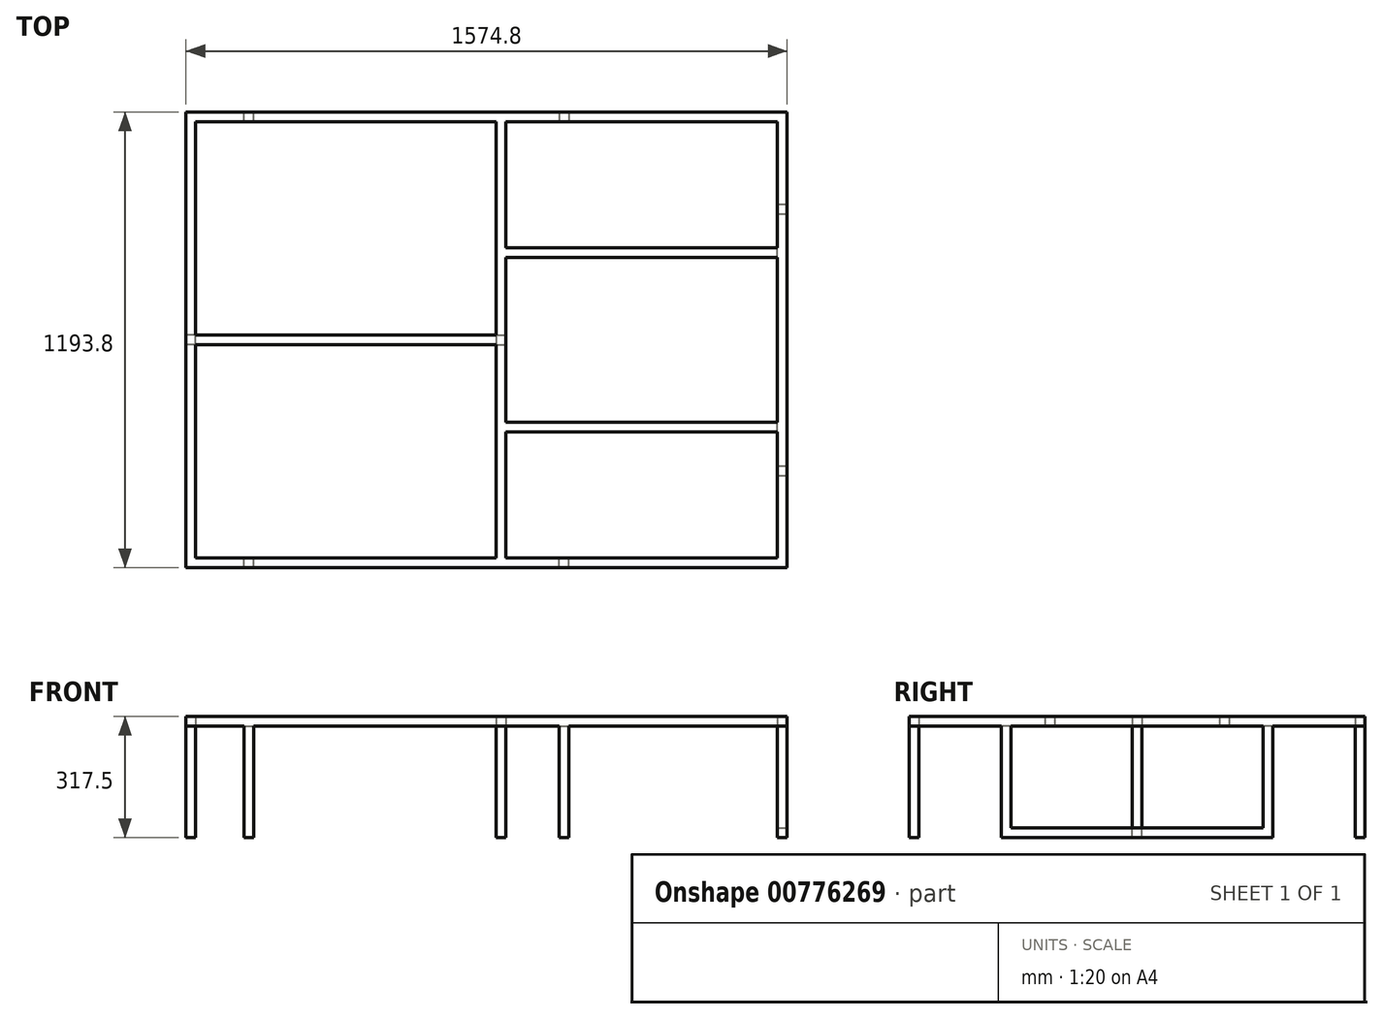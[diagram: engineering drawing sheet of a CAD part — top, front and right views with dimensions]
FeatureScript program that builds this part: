
annotation { "Feature Type Name" : "Feature", "Feature Type Description" : "" }
export const myFeature = defineFeature(function(context is Context, id is Id, definition is map)
    precondition{}
    {
        {
            var Q0;
            Q0=qCreatedBy(makeId("Top.planeOp"),FACE);
            var sketch = newSketch(context, id + "F0", { "sketchPlane" : qUnion([Q0])});
            skLineSegment(sketch, "E0.bottom", {"start": v(-787.4, 596.9) * mm, "end": v(787.4, 596.9) * mm});
            skLineSegment(sketch, "E0.top", {"start": v(-787.4, -596.9) * mm, "end": v(787.4, -596.9) * mm});
            skLineSegment(sketch, "E0.left", {"start": v(-787.4, 596.9) * mm, "end": v(-787.4, -596.9) * mm});
            skLineSegment(sketch, "E0.right", {"start": v(787.4, 596.9) * mm, "end": v(787.4, -596.9) * mm});
            skSolve(sketch);
        }
        {
            var Q0;
            Q0 = qSketchRegion(id + "F0", true);
            extrude(context, id + "F1", {"entities" : qUnion([Q0]), "depth" : 25.4 * mm, "offsetDistance" : 25.4 * mm});
        }
        {
            var Q0;
            Q0=makeQuery(id+"F1.opExtrude","CAP_FACE",FACE,{"disambiguationData":[OSD([sQuery(id+"F0.wireOp",EDGE,"E0.bottom"),sQuery(id+"F0.wireOp",EDGE,"E0.top"),sQuery(id+"F0.wireOp",EDGE,"E0.left"),sQuery(id+"F0.wireOp",EDGE,"E0.right")])],"isStart":true});
            var sketch = newSketch(context, id + "F2", { "sketchPlane" : qUnion([Q0])});
            skLineSegment(sketch, "E1.bottom", {"start": v(-762, -571.5) * mm, "end": v(25.4, -571.5) * mm});
            skLineSegment(sketch, "E1.top", {"start": v(-762, 571.5) * mm, "end": v(25.4, 571.5) * mm});
            skLineSegment(sketch, "E1.left", {"start": v(-762, -571.5) * mm, "end": v(-762, -12.7) * mm});
            skLineSegment(sketch, "E1.right", {"start": v(25.4, -571.5) * mm, "end": v(25.4, -12.7) * mm});
            skLineSegment(sketch, "E2.bottom", {"start": v(50.8, -571.5) * mm, "end": v(762, -571.5) * mm});
            skLineSegment(sketch, "E2.top", {"start": v(50.8, -241.3) * mm, "end": v(762, -241.3) * mm});
            skLineSegment(sketch, "E2.left", {"start": v(50.8, -571.5) * mm, "end": v(50.8, -241.3) * mm});
            skLineSegment(sketch, "E2.right", {"start": v(762, -571.5) * mm, "end": v(762, -241.3) * mm});
            skLineSegment(sketch, "E3.bottom", {"start": v(50.8, -215.9) * mm, "end": v(762, -215.9) * mm});
            skLineSegment(sketch, "E3.top", {"start": v(50.8, 215.9) * mm, "end": v(762, 215.9) * mm});
            skLineSegment(sketch, "E3.left", {"start": v(50.8, -215.9) * mm, "end": v(50.8, 215.9) * mm});
            skLineSegment(sketch, "E3.right", {"start": v(762, -215.9) * mm, "end": v(762, 215.9) * mm});
            skLineSegment(sketch, "E4.bottom", {"start": v(50.8, 241.3) * mm, "end": v(762, 241.3) * mm});
            skLineSegment(sketch, "E4.top", {"start": v(50.8, 571.5) * mm, "end": v(762, 571.5) * mm});
            skLineSegment(sketch, "E4.left", {"start": v(50.8, 241.3) * mm, "end": v(50.8, 571.5) * mm});
            skLineSegment(sketch, "E4.right", {"start": v(762, 241.3) * mm, "end": v(762, 571.5) * mm});
            skLineSegment(sketch, "E5", {"start": v(-762, -12.7) * mm, "end": v(25.4, -12.7) * mm});
            skLineSegment(sketch, "E6", {"start": v(-762, 12.7) * mm, "end": v(25.4, 12.7) * mm});
            skLineSegment(sketch, "E7.trimOffspring", {"start": v(-762, 12.7) * mm, "end": v(-762, 571.5) * mm});
            skLineSegment(sketch, "E8.trimOffspring", {"start": v(25.4, 12.7) * mm, "end": v(25.4, 571.5) * mm});
            skSolve(sketch);
        }
        {
            var Q0;
            Q0 = qSketchRegion(id + "F2", true);
            extrude(context, id + "F3", {"entities" : qUnion([Q0]), "operationType" : NewBodyOperationType.REMOVE, "endBound" : BoundingType.THROUGH_ALL, "oppositeDirection" : true, "depth" : 25.4 * mm, "offsetDistance" : 25.4 * mm});
        }
        {
            var Q0;
            Q0=makeQuery(id+"F1.opExtrude","CAP_FACE",FACE,{"disambiguationData":[OSD([sQuery(id+"F0.wireOp",EDGE,"E0.bottom"),sQuery(id+"F0.wireOp",EDGE,"E0.top"),sQuery(id+"F0.wireOp",EDGE,"E0.left"),sQuery(id+"F0.wireOp",EDGE,"E0.right")])],"isStart":true});
            var sketch = newSketch(context, id + "F4", { "sketchPlane" : qUnion([Q0])});
            skLineSegment(sketch, "E9.bottom", {"start": v(-635, 596.9) * mm, "end": v(-609.6, 596.9) * mm});
            skLineSegment(sketch, "E9.top", {"start": v(-635, 571.5) * mm, "end": v(-609.6, 571.5) * mm});
            skLineSegment(sketch, "E9.left", {"start": v(-635, 596.9) * mm, "end": v(-635, 571.5) * mm});
            skLineSegment(sketch, "E9.right", {"start": v(-609.6, 596.9) * mm, "end": v(-609.6, 571.5) * mm});
            skLineSegment(sketch, "E10.bottom", {"start": v(-635, -571.5) * mm, "end": v(-609.6, -571.5) * mm});
            skLineSegment(sketch, "E10.top", {"start": v(-635, -596.9) * mm, "end": v(-609.6, -596.9) * mm});
            skLineSegment(sketch, "E10.left", {"start": v(-635, -571.5) * mm, "end": v(-635, -596.9) * mm});
            skLineSegment(sketch, "E10.right", {"start": v(-609.6, -571.5) * mm, "end": v(-609.6, -596.9) * mm});
            skLineSegment(sketch, "E11.bottom", {"start": v(-762, 12.7) * mm, "end": v(-787.4, 12.7) * mm});
            skLineSegment(sketch, "E11.top", {"start": v(-762, -12.7) * mm, "end": v(-787.4, -12.7) * mm});
            skLineSegment(sketch, "E11.left", {"start": v(-762, 12.7) * mm, "end": v(-762, -12.7) * mm});
            skLineSegment(sketch, "E11.right", {"start": v(-787.4, 12.7) * mm, "end": v(-787.4, -12.7) * mm});
            skLineSegment(sketch, "E12.bottom", {"start": v(25.4, -12.7) * mm, "end": v(50.8, -12.7) * mm});
            skLineSegment(sketch, "E12.top", {"start": v(25.4, 12.7) * mm, "end": v(50.8, 12.7) * mm});
            skLineSegment(sketch, "E12.left", {"start": v(25.4, -12.7) * mm, "end": v(25.4, 12.7) * mm});
            skLineSegment(sketch, "E12.right", {"start": v(50.8, -12.7) * mm, "end": v(50.8, 12.7) * mm});
            skLineSegment(sketch, "E13.bottom", {"start": v(762, 355.6) * mm, "end": v(787.4, 355.6) * mm});
            skLineSegment(sketch, "E13.top", {"start": v(762, -355.6) * mm, "end": v(787.4, -355.6) * mm});
            skLineSegment(sketch, "E13.left", {"start": v(762, 355.6) * mm, "end": v(762, -355.6) * mm});
            skLineSegment(sketch, "E13.right", {"start": v(787.4, 355.6) * mm, "end": v(787.4, -355.6) * mm});
            skLineSegment(sketch, "E14.bottom", {"start": v(190.5, 596.9) * mm, "end": v(215.9, 596.9) * mm});
            skLineSegment(sketch, "E14.top", {"start": v(190.5, 571.5) * mm, "end": v(215.9, 571.5) * mm});
            skLineSegment(sketch, "E14.left", {"start": v(190.5, 596.9) * mm, "end": v(190.5, 571.5) * mm});
            skLineSegment(sketch, "E14.right", {"start": v(215.9, 596.9) * mm, "end": v(215.9, 571.5) * mm});
            skLineSegment(sketch, "E15.bottom", {"start": v(190.5, -596.9) * mm, "end": v(215.9, -596.9) * mm});
            skLineSegment(sketch, "E15.top", {"start": v(190.5, -571.5) * mm, "end": v(215.9, -571.5) * mm});
            skLineSegment(sketch, "E15.left", {"start": v(190.5, -596.9) * mm, "end": v(190.5, -571.5) * mm});
            skLineSegment(sketch, "E15.right", {"start": v(215.9, -596.9) * mm, "end": v(215.9, -571.5) * mm});
            skSolve(sketch);
        }
        {
            var Q0;
            Q0 = qSketchRegion(id + "F4", true);
            extrude(context, id + "F5", {"entities" : qUnion([Q0]), "operationType" : NewBodyOperationType.ADD, "depth" : 292.1 * mm, "offsetDistance" : 25.4 * mm});
        }
        {
            var Q0;
            Q0=makeQuery(id+"F5.boolean.opBoolean","MERGE",FACE,{"derivedFrom":[makeQuery(id+"F1.opExtrude","SWEPT_FACE",FACE,{"disambiguationData":[OSD([sQuery(id+"F0.wireOp",EDGE,"E0.right")])]}),makeQuery(id+"F5.opExtrude","SWEPT_FACE",FACE,{"disambiguationData":[OSD([sQuery(id+"F4.wireOp",EDGE,"E13.right")])]})]});
            var sketch = newSketch(context, id + "F6", { "sketchPlane" : qUnion([Q0])});
            skLineSegment(sketch, "E16.bottom", {"start": v(-330.2, -266.7) * mm, "end": v(330.2, -266.7) * mm});
            skLineSegment(sketch, "E16.top", {"start": v(-330.2, 0) * mm, "end": v(330.2, 0) * mm});
            skLineSegment(sketch, "E16.left", {"start": v(-330.2, -266.7) * mm, "end": v(-330.2, 0) * mm});
            skLineSegment(sketch, "E16.right", {"start": v(330.2, -266.7) * mm, "end": v(330.2, 0) * mm});
            skSolve(sketch);
        }
        {
            var Q0;
            Q0 = qSketchRegion(id + "F6", true);
            extrude(context, id + "F7", {"entities" : qUnion([Q0]), "operationType" : NewBodyOperationType.REMOVE, "oppositeDirection" : true, "depth" : 50.8 * mm, "offsetDistance" : 25.4 * mm});
        }
    });
